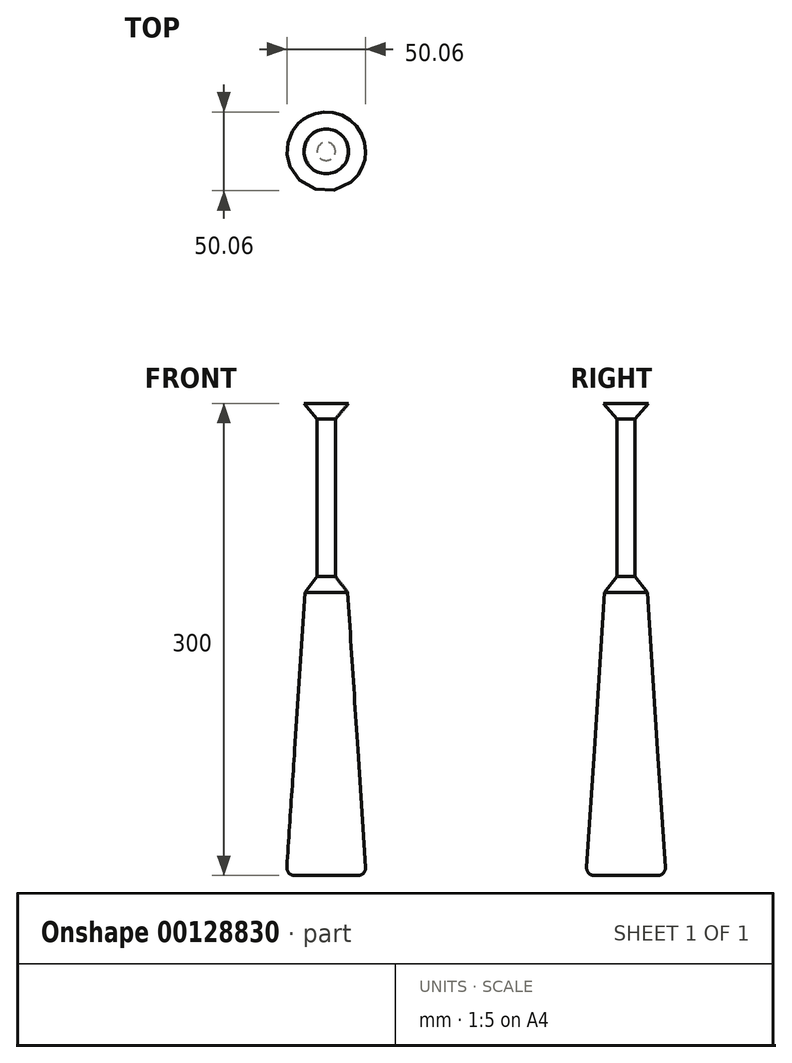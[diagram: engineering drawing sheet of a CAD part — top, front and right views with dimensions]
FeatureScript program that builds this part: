
annotation { "Feature Type Name" : "Feature", "Feature Type Description" : "" }
export const myFeature = defineFeature(function(context is Context, id is Id, definition is map)
    precondition{}
    {
        {
            var Q0;
            Q0=qCreatedBy(makeId("Top.planeOp"),FACE);
            var sketch = newSketch(context, id + "F0", { "sketchPlane" : qUnion([Q0])});
            skCircle(sketch, "E0", {"center": v(0, 0) * mm, "radius": 14.2 * mm});
            skSolve(sketch);
        }
        {
            var Q0;
            Q0=qCreatedBy(makeId("Top.planeOp"),FACE);
            cPlane(context, id + "F1", {"entities" : qUnion([Q0]), "cplaneType" : CPlaneType.OFFSET, "offset" : 10 * mm, "oppositeDirection" : true, "width" : 150 * mm, "height" : 150 * mm});
        }
        {
            var Q0;
            Q0=qCreatedBy(id+"F1.planeOp",FACE);
            cPlane(context, id + "F2", {"entities" : qUnion([Q0]), "cplaneType" : CPlaneType.OFFSET, "offset" : 100 * mm, "oppositeDirection" : true, "width" : 150 * mm, "height" : 150 * mm});
        }
        {
            var Q0;
            Q0=qCreatedBy(id+"F2.planeOp",FACE);
            cPlane(context, id + "F3", {"entities" : qUnion([Q0]), "cplaneType" : CPlaneType.OFFSET, "offset" : 10 * mm, "oppositeDirection" : true, "width" : 150 * mm, "height" : 150 * mm});
        }
        {
            var Q0;
            Q0=qCreatedBy(id+"F3.planeOp",FACE);
            cPlane(context, id + "F4", {"entities" : qUnion([Q0]), "cplaneType" : CPlaneType.OFFSET, "offset" : 100 * mm, "oppositeDirection" : true, "width" : 150 * mm, "height" : 150 * mm});
        }
        {
            var Q0;
            Q0=qCreatedBy(id+"F1.planeOp",FACE);
            var sketch = newSketch(context, id + "F5", { "sketchPlane" : qUnion([Q0])});
            skCircle(sketch, "E1", {"center": v(0, 0) * mm, "radius": 5.8 * mm});
            skSolve(sketch);
        }
        {
            var Q0;
            Q0=qCreatedBy(id+"F2.planeOp",FACE);
            var sketch = newSketch(context, id + "F6", { "sketchPlane" : qUnion([Q0])});
            skCircle(sketch, "E2", {"center": v(0, 0) * mm, "radius": 5.81 * mm});
            skSolve(sketch);
        }
        {
            var Q0;
            Q0=qCreatedBy(id+"F3.planeOp",FACE);
            var sketch = newSketch(context, id + "F7", { "sketchPlane" : qUnion([Q0])});
            skCircle(sketch, "E3", {"center": v(0, 0) * mm, "radius": 13.57 * mm});
            skSolve(sketch);
        }
        {
            var Q0;
            Q0=qCreatedBy(id+"F4.planeOp",FACE);
            var sketch = newSketch(context, id + "F8", { "sketchPlane" : qUnion([Q0])});
            skCircle(sketch, "E4", {"center": v(0, 0) * mm, "radius": 20.06 * mm});
            skSolve(sketch);
        }
        {
            var Q0;
            Q0 = qSketchRegion(id + "F0", true);
            var Q1;
            Q1 = qSketchRegion(id + "F5", true);
            loft(context, id + "F9", {"sheetProfilesArray" : [{ "sheetProfileEntities" : qUnion([Q0]) }, { "sheetProfileEntities" : qUnion([Q1]) }]});
        }
        {
            var Q1;
            Q1 = qSketchRegion(id + "F5", true);
            var Q2;
            Q2 = qSketchRegion(id + "F6", true);
            loft(context, id + "F10", {"operationType" : NewBodyOperationType.ADD, "sheetProfilesArray" : [{ "sheetProfileEntities" : qUnion([Q1]) }, { "sheetProfileEntities" : qUnion([Q2]) }]});
        }
        {
            var Q1;
            Q1 = qSketchRegion(id + "F6", true);
            var Q2;
            Q2 = qSketchRegion(id + "F7", true);
            loft(context, id + "F11", {"operationType" : NewBodyOperationType.ADD, "sheetProfilesArray" : [{ "sheetProfileEntities" : qUnion([Q1]) }, { "sheetProfileEntities" : qUnion([Q2]) }]});
        }
        {
            var Q1;
            Q1 = qSketchRegion(id + "F7", true);
            var Q2;
            Q2 = qSketchRegion(id + "F8", true);
            loft(context, id + "F12", {"operationType" : NewBodyOperationType.ADD, "sheetProfilesArray" : [{ "sheetProfileEntities" : qUnion([Q1]) }, { "sheetProfileEntities" : qUnion([Q2]) }]});
        }
        {
            var Q0;
            Q0=qCreatedBy(id+"F4.planeOp",FACE);
            cPlane(context, id + "F13", {"entities" : qUnion([Q0]), "cplaneType" : CPlaneType.OFFSET, "offset" : 80 * mm, "oppositeDirection" : true, "width" : 150 * mm, "height" : 150 * mm});
        }
        {
            var Q0;
            Q0=qCreatedBy(id+"F13.planeOp",FACE);
            var sketch = newSketch(context, id + "F14", { "sketchPlane" : qUnion([Q0])});
            skCircle(sketch, "E5", {"center": v(0, 0) * mm, "radius": 25.38 * mm});
            skSolve(sketch);
        }
        {
            var Q1;
            Q1 = qSketchRegion(id + "F8", true);
            var Q2;
            Q2 = qSketchRegion(id + "F14", true);
            loft(context, id + "F15", {"operationType" : NewBodyOperationType.ADD, "sheetProfilesArray" : [{ "sheetProfileEntities" : qUnion([Q1]) }, { "sheetProfileEntities" : qUnion([Q2]) }]});
        }
        {
            var Q0;
            Q0=makeQuery(id+"F15.opLoft","MID_CAP_EDGE",EDGE,{"disambiguationData":[OSD([sQuery(id+"F8.wireOp",EDGE,"E4"),sQuery(id+"F14.wireOp",EDGE,"E5")])],"capPos":1.0});
            fillet(context, id + "F16", {"entities" : qUnion([Q0]), "radius" : 5 * mm, "tangentPropagation" : true, "allowEdgeOverflow" : false});
        }
    });
